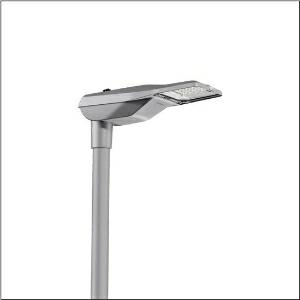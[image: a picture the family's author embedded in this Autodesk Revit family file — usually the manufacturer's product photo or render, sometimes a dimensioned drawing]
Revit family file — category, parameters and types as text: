
# Revit family: streetlight_sl_21_micro___pl52_5xe1h43s08db_6aa2
name_source: partatom
category: Lighting Fixtures
units: mm (PartAtom-declared; Revit-internal decimal feet)

## family parameters
Cut with Voids When Loaded = No
Host = Face
Light Source = No
Part Type = Normal
Room Calculation Point = No
Round Connector Dimension = Use Diameter
Shared = No

## types (1)
- --- (1 x LED, 5230 lm, 39.1 W, 4000K)
    Apparent Load = 39 VA
    CIE Flux Codes = 27 59 98 100 100
    Color Rendering = 70
    Color Temperature = 4000K
    Default Elevation = 1800 mm
    Description = Streetlight SL 21 micro, mast luminaire, primary light control with lens, of PMMA, primary optical cover: cover, of toughened safety glass, transparent, light distribution: PL52, light emission: direct distribution, primary light characteristic: asymmetric, installation type: side-entry, post-top, LED, High Power LED, rated luminous flux: 5.230lm, luminous efficacy: 134lm/W, light colour: 740, colour temperature: 4000K, control gear: D4i, control: flexible luminous flux parameterisation, time-dependent luminous flux control, constant luminous flux control, overheat protection, pre-setting: logarithmic dimming characteristic, mains connection: 220..240V, AC, 50/60Hz, start of lifetime: 39W, end of service life: 41W, reduction: 18W, luminaire housing, of diecast aluminium, powder-coated, Siteco® metallic grey (DB 702S), corrosivity category C5 mid according to DIN EN ISO 12944, please order mast flange separately, inclination adjustable: 0°, 5°, 10°, 15°, sealing non-destructively replaceable, multi-level sealing system, length: 528mm, width: 235mm, height: 110mm, mast flange for spigot size: 42mm (side-entry): 5XC10008XM4, 60/48mm (side-entry/post-top): 5XC10108XM2, 76/60mm (side-entry/post-top): 5XC10108XM1, Smart Interface above, protection rating (complete): IP66, insulation class (complete): insulation class II (safety insulation), certification: CE, ENEC, ENEC+, VDE, impact resistance: IK10, permissible operating ambient temperature for outdoor applications: -40..+50°C, standard-compliant lighting for roads and squares, packaging unit: 1 piece

Light Distribution: PL52
    Height = 110 mm
    Lamp = 1 x LED
    Lamp Light Flux = 5230 lm
    Lamp Power = 39.1 W
    Lamp count = 1
    Length = 528 mm
    Luminous efficacy = 134 lm/W
    Manufacturer = Siteco
    ModVariant = No
    Model = 5XE1H43S08DB
    Number of Poles = 1
    OnlyDefault = Yes
    Power Factor = 1
    Product Name = Streetlight SL 21 micro | PL52
    Product group = mast luminaire | pylon top
    ProductGroupID = 6100
    Protection Class = Protection class II
    Protection Degree = IP 66
    RLX_Detail_Level = 1
    RLX_Emergency_Light_Flux = 0 lm
    RLX_Emergency_Type = 0
    RLX_Emergency_Type_DB = No
    RlxData = <blob elided: 107933 chars, md5=604201ef>
    Socket = socket
    Standby Power = 0 W
    System Light Flux = 5230 lm
    System Power = 39 W
    Type Comments = factory setting: luminous flux: 100 % | dim-lin: 254 | 765 mA
    Type Image = l_1277292.jpg
    URL = http://relux.com
    VarID = @adj_177691
    Voltage = 0 V
    Weight = 0.00 kg
    Width = 235 mm

## geometry (parser evidence)
native form markers: Blend x4, Sweep x11
no freeform markers — native parametric forms only
